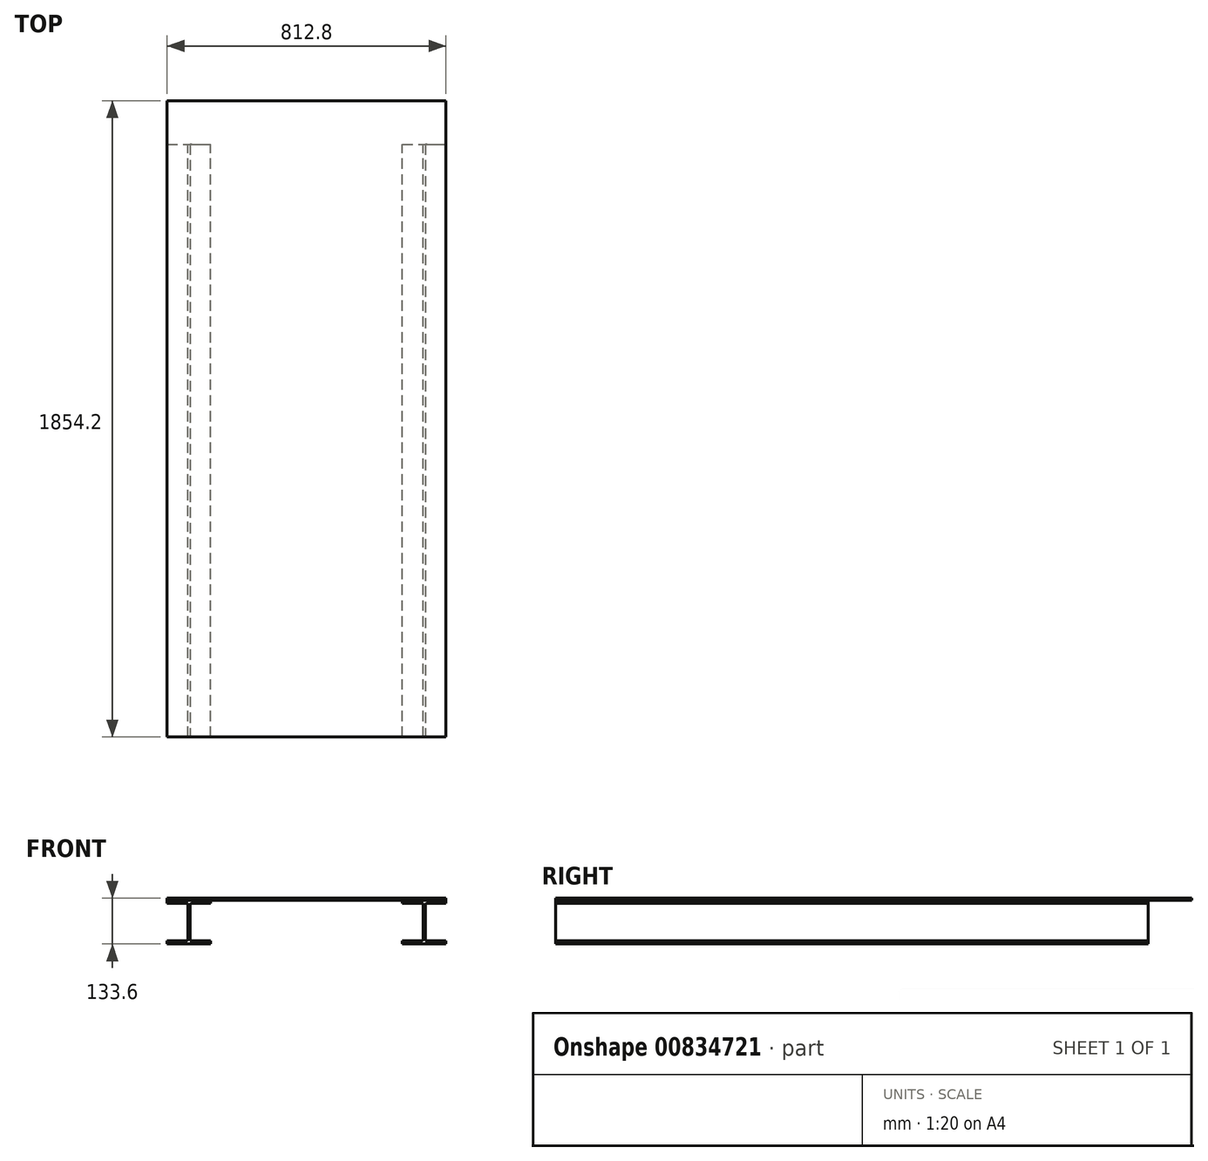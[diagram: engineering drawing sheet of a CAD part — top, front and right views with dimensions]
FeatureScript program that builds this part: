
annotation { "Feature Type Name" : "Feature", "Feature Type Description" : "" }
export const myFeature = defineFeature(function(context is Context, id is Id, definition is map)
    precondition{}
    {
        {
            var Q0;
            Q0=qCreatedBy(makeId("Top.planeOp"),FACE);
            var sketch = newSketch(context, id + "F0", { "sketchPlane" : qUnion([Q0])});
            skLineSegment(sketch, "E0", {"start": v(-404.4, 1266.5) * mm, "end": v(408.4, 1266.5) * mm});
            skLineSegment(sketch, "E1", {"start": v(-404.4, 1266.5) * mm, "end": v(-404.4, -587.7) * mm});
            skLineSegment(sketch, "E2", {"start": v(408.4, 1266.5) * mm, "end": v(408.4, -587.7) * mm});
            skLineSegment(sketch, "E3", {"start": v(408.4, -587.7) * mm, "end": v(-404.4, -587.7) * mm});
            skSolve(sketch);
        }
        {
            var Q0;
            Q0=makeQuery(id+"F0.imprint","IMPRINT",FACE,{"disambiguationData":[TD([[makeQuery(id+"F0.imprint","IMPRINT",EDGE,{"derivedFrom":sQuery(id+"F0.wireOp",EDGE,"E0")}),-1.0]])]});
            extrude(context, id + "F1", {"entities" : qUnion([Q0]), "depth" : 6.35 * mm, "offsetDistance" : 25.4 * mm});
        }
        {
            var Q0;
            Q0=makeQuery(id+"F1.opExtrude","CAP_FACE",FACE,{"disambiguationData":[OSD([sQuery(id+"F0.wireOp",EDGE,"E0"),sQuery(id+"F0.wireOp",EDGE,"E1"),sQuery(id+"F0.wireOp",EDGE,"E2"),sQuery(id+"F0.wireOp",EDGE,"E3")])],"isStart":true});
            var sketch = newSketch(context, id + "F2", { "sketchPlane" : qUnion([Q0])});
            skLineSegment(sketch, "E4", {"start": v(-404.4, 587.7) * mm, "end": v(-277.4, 587.7) * mm});
            skLineSegment(sketch, "E5", {"start": v(408.4, 587.7) * mm, "end": v(281.4, 587.7) * mm});
            skLineSegment(sketch, "E6", {"start": v(-404.4, -1139.5) * mm, "end": v(-277.4, -1139.5) * mm});
            skLineSegment(sketch, "E7", {"start": v(-404.4, 587.7) * mm, "end": v(-404.4, -1139.5) * mm});
            skLineSegment(sketch, "E8", {"start": v(-277.4, 587.7) * mm, "end": v(-277.4, -1139.5) * mm});
            skSolve(sketch);
        }
        {
            var Q0;
            Q0 = qSketchRegion(id + "F2", true);
            extrude(context, id + "F3", {"entities" : qUnion([Q0]), "depth" : 9.14 * mm, "offsetDistance" : 25.4 * mm});
        }
        {
            var Q0;
            Q0=makeQuery(id+"F3.opExtrude","CAP_FACE",FACE,{"disambiguationData":[OSD([sQuery(id+"F2.wireOp",EDGE,"E4"),sQuery(id+"F2.wireOp",EDGE,"E6"),sQuery(id+"F2.wireOp",EDGE,"E7"),sQuery(id+"F2.wireOp",EDGE,"E8")])],"isStart":false});
            var sketch = newSketch(context, id + "F4", { "sketchPlane" : qUnion([Q0])});
            skLineSegment(sketch, "E9", {"start": v(-340.9, 587.7) * mm, "end": v(-343.94, 587.7) * mm});
            skLineSegment(sketch, "E10", {"start": v(-340.9, 587.7) * mm, "end": v(-337.85, 587.7) * mm});
            skLineSegment(sketch, "E11", {"start": v(-343.94, 587.7) * mm, "end": v(-343.94, -1139.5) * mm});
            skLineSegment(sketch, "E12", {"start": v(-343.94, -1139.5) * mm, "end": v(-337.85, -1139.5) * mm});
            skLineSegment(sketch, "E13", {"start": v(-337.85, -1139.5) * mm, "end": v(-337.85, 587.7) * mm});
            skLineSegment(sketch, "E14", {"start": v(-337.85, 587.7) * mm, "end": v(-343.94, 587.7) * mm});
            skSolve(sketch);
        }
        {
            var Q0;
            Q0 = qSketchRegion(id + "F4", true);
            extrude(context, id + "F5", {"entities" : qUnion([Q0]), "operationType" : NewBodyOperationType.ADD, "depth" : 108.97 * mm, "offsetDistance" : 25.4 * mm});
        }
        {
            var Q0;
            Q0=makeQuery(id+"F5.opExtrude","CAP_FACE",FACE,{"disambiguationData":[OSD([sQuery(id+"F4.wireOp",EDGE,"E11"),sQuery(id+"F4.wireOp",EDGE,"E12"),sQuery(id+"F4.wireOp",EDGE,"E13"),sQuery(id+"F4.wireOp",EDGE,"E14")])],"isStart":false});
            var sketch = newSketch(context, id + "F6", { "sketchPlane" : qUnion([Q0])});
            skLineSegment(sketch, "E15", {"start": v(-340.9, 587.7) * mm, "end": v(-277.4, 587.7) * mm});
            skLineSegment(sketch, "E16", {"start": v(-340.9, 587.7) * mm, "end": v(-404.4, 587.7) * mm});
            skLineSegment(sketch, "E17", {"start": v(-404.4, 587.7) * mm, "end": v(-404.4, -1139.5) * mm});
            skLineSegment(sketch, "E18", {"start": v(-404.4, -1139.5) * mm, "end": v(-277.4, -1139.5) * mm});
            skLineSegment(sketch, "E19", {"start": v(-277.4, -1139.5) * mm, "end": v(-277.4, 587.7) * mm});
            skLineSegment(sketch, "E20", {"start": v(-404.4, 587.7) * mm, "end": v(-277.4, 587.7) * mm});
            skSolve(sketch);
        }
        {
            var Q0;
            Q0 = qSketchRegion(id + "F6", true);
            extrude(context, id + "F7", {"entities" : qUnion([Q0]), "operationType" : NewBodyOperationType.ADD, "depth" : 9.14 * mm, "offsetDistance" : 25.4 * mm});
        }
        {
            var Q0;
            Q0=makeQuery(id+"F1.opExtrude","CAP_FACE",FACE,{"disambiguationData":[OSD([sQuery(id+"F0.wireOp",EDGE,"E0"),sQuery(id+"F0.wireOp",EDGE,"E1"),sQuery(id+"F0.wireOp",EDGE,"E2"),sQuery(id+"F0.wireOp",EDGE,"E3")])],"isStart":true});
            var sketch = newSketch(context, id + "F8", { "sketchPlane" : qUnion([Q0])});
            skLineSegment(sketch, "E21", {"start": v(408.4, 587.7) * mm, "end": v(281.4, 587.7) * mm});
            skLineSegment(sketch, "E22", {"start": v(281.4, 587.7) * mm, "end": v(281.4, -1139.5) * mm});
            skLineSegment(sketch, "E23", {"start": v(281.4, -1139.5) * mm, "end": v(408.4, -1139.5) * mm});
            skLineSegment(sketch, "E24", {"start": v(408.4, -1139.5) * mm, "end": v(408.4, 587.7) * mm});
            skSolve(sketch);
        }
        {
            var Q0;
            Q0 = qSketchRegion(id + "F8", true);
            extrude(context, id + "F9", {"entities" : qUnion([Q0]), "depth" : 9.14 * mm, "offsetDistance" : 25.4 * mm});
        }
        {
            var Q0;
            Q0=makeQuery(id+"F9.opExtrude","CAP_FACE",FACE,{"disambiguationData":[OSD([sQuery(id+"F8.wireOp",EDGE,"E21"),sQuery(id+"F8.wireOp",EDGE,"E22"),sQuery(id+"F8.wireOp",EDGE,"E23"),sQuery(id+"F8.wireOp",EDGE,"E24")])],"isStart":false});
            var sketch = newSketch(context, id + "F10", { "sketchPlane" : qUnion([Q0])});
            skLineSegment(sketch, "E25", {"start": v(344.9, 587.7) * mm, "end": v(347.95, 587.7) * mm});
            skLineSegment(sketch, "E26", {"start": v(344.9, 587.7) * mm, "end": v(341.86, 587.7) * mm});
            skLineSegment(sketch, "E27", {"start": v(341.86, 587.7) * mm, "end": v(341.86, -1139.5) * mm});
            skPoint(sketch, "E27.endSnap0", {"position": v(344.9, -1139.5) * mm});
            skLineSegment(sketch, "E28", {"start": v(341.86, -1139.5) * mm, "end": v(347.95, -1139.5) * mm});
            skLineSegment(sketch, "E29", {"start": v(347.95, -1139.5) * mm, "end": v(347.95, 587.7) * mm});
            skLineSegment(sketch, "E30", {"start": v(341.86, 587.7) * mm, "end": v(347.95, 587.7) * mm});
            skSolve(sketch);
        }
        {
            var Q0;
            Q0 = qSketchRegion(id + "F10", true);
            extrude(context, id + "F11", {"entities" : qUnion([Q0]), "operationType" : NewBodyOperationType.ADD, "depth" : 108.97 * mm, "offsetDistance" : 25.4 * mm});
        }
        {
            var Q0;
            Q0=makeQuery(id+"F11.opExtrude","CAP_FACE",FACE,{"disambiguationData":[OSD([sQuery(id+"F10.wireOp",EDGE,"E27"),sQuery(id+"F10.wireOp",EDGE,"E28"),sQuery(id+"F10.wireOp",EDGE,"E29"),sQuery(id+"F10.wireOp",EDGE,"E30")])],"isStart":false});
            var sketch = newSketch(context, id + "F12", { "sketchPlane" : qUnion([Q0])});
            skLineSegment(sketch, "E31", {"start": v(344.9, 587.7) * mm, "end": v(408.4, 587.7) * mm});
            skLineSegment(sketch, "E32", {"start": v(344.9, 587.7) * mm, "end": v(281.4, 587.7) * mm});
            skLineSegment(sketch, "E33", {"start": v(281.4, 587.7) * mm, "end": v(281.4, -1139.5) * mm});
            skLineSegment(sketch, "E34", {"start": v(281.4, -1139.5) * mm, "end": v(408.4, -1139.5) * mm});
            skLineSegment(sketch, "E35", {"start": v(408.4, -1139.5) * mm, "end": v(408.4, 587.7) * mm});
            skLineSegment(sketch, "E36", {"start": v(281.4, 587.7) * mm, "end": v(408.4, 587.7) * mm});
            skSolve(sketch);
        }
        {
            var Q0;
            Q0 = qSketchRegion(id + "F12", true);
            extrude(context, id + "F13", {"entities" : qUnion([Q0]), "operationType" : NewBodyOperationType.ADD, "depth" : 9.14 * mm, "offsetDistance" : 25.4 * mm});
        }
        {
            var Q0;
            Q0=makeQuery(id+"F5.opExtrude","CAP_EDGE",EDGE,{"disambiguationData":[OSD([sQuery(id+"F4.wireOp",EDGE,"E11")])],"isStart":true});
            var Q1;
            Q1=makeQuery(id+"F5.opExtrude","CAP_EDGE",EDGE,{"disambiguationData":[OSD([sQuery(id+"F4.wireOp",EDGE,"E11")])],"isStart":false});
            var Q2;
            Q2=makeQuery(id+"F5.opExtrude","CAP_EDGE",EDGE,{"disambiguationData":[OSD([sQuery(id+"F4.wireOp",EDGE,"E13")])],"isStart":false});
            var Q3;
            Q3=makeQuery(id+"F5.opExtrude","CAP_EDGE",EDGE,{"disambiguationData":[OSD([sQuery(id+"F4.wireOp",EDGE,"E13")])],"isStart":true});
            fillet(context, id + "F14", {"entities" : qUnion([Q0, Q1, Q2, Q3]), "radius" : 5.08 * mm, "tangentPropagation" : true, "allowEdgeOverflow" : false});
        }
        {
            var Q0;
            Q0=makeQuery(id+"F11.opExtrude","CAP_EDGE",EDGE,{"disambiguationData":[OSD([sQuery(id+"F10.wireOp",EDGE,"E29")])],"isStart":true});
            var Q1;
            Q1=makeQuery(id+"F11.opExtrude","CAP_EDGE",EDGE,{"disambiguationData":[OSD([sQuery(id+"F10.wireOp",EDGE,"E29")])],"isStart":false});
            var Q2;
            Q2=makeQuery(id+"F11.opExtrude","CAP_EDGE",EDGE,{"disambiguationData":[OSD([sQuery(id+"F10.wireOp",EDGE,"E27")])],"isStart":true});
            var Q3;
            Q3=makeQuery(id+"F11.opExtrude","CAP_EDGE",EDGE,{"disambiguationData":[OSD([sQuery(id+"F10.wireOp",EDGE,"E27")])],"isStart":false});
            fillet(context, id + "F15", {"entities" : qUnion([Q0, Q1, Q2, Q3]), "radius" : 5.08 * mm, "tangentPropagation" : true, "allowEdgeOverflow" : false});
        }
    });
